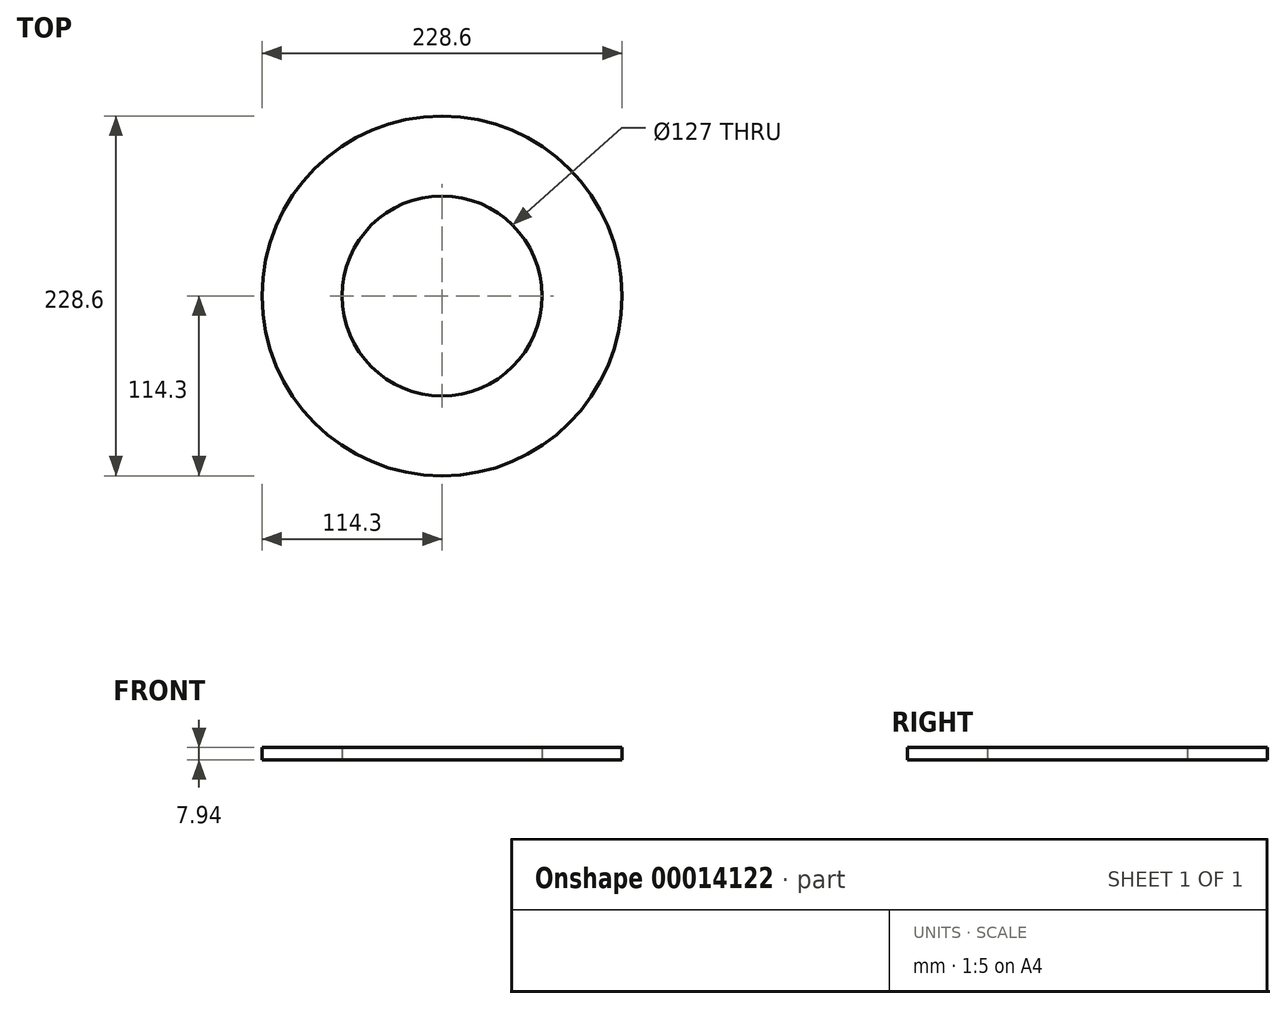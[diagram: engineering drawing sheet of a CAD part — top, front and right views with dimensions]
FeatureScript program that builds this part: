
annotation { "Feature Type Name" : "Feature", "Feature Type Description" : "" }
export const myFeature = defineFeature(function(context is Context, id is Id, definition is map)
    precondition{}
    {
        {
            var Q0;
            Q0=qCreatedBy(makeId("Top.planeOp"),FACE);
            var sketch = newSketch(context, id + "F0", { "sketchPlane" : qUnion([Q0])});
            skCircle(sketch, "E0", {"center": v(0, 0) * mm, "radius": 114.3 * mm});
            skCircle(sketch, "E1", {"center": v(0, 0) * mm, "radius": 63.5 * mm});
            skSolve(sketch);
        }
        {
            var Q0;
            Q0=makeQuery(id+"F0.imprint","IMPRINT",FACE,{"disambiguationData":[TD([[makeQuery(id+"F0.imprint","IMPRINT",EDGE,{"derivedFrom":sQuery(id+"F0.wireOp",EDGE,"E0")}),1.0]])]});
            extrude(context, id + "F1", {"entities" : qUnion([Q0]), "depth" : 7.94 * mm});
        }
    });
